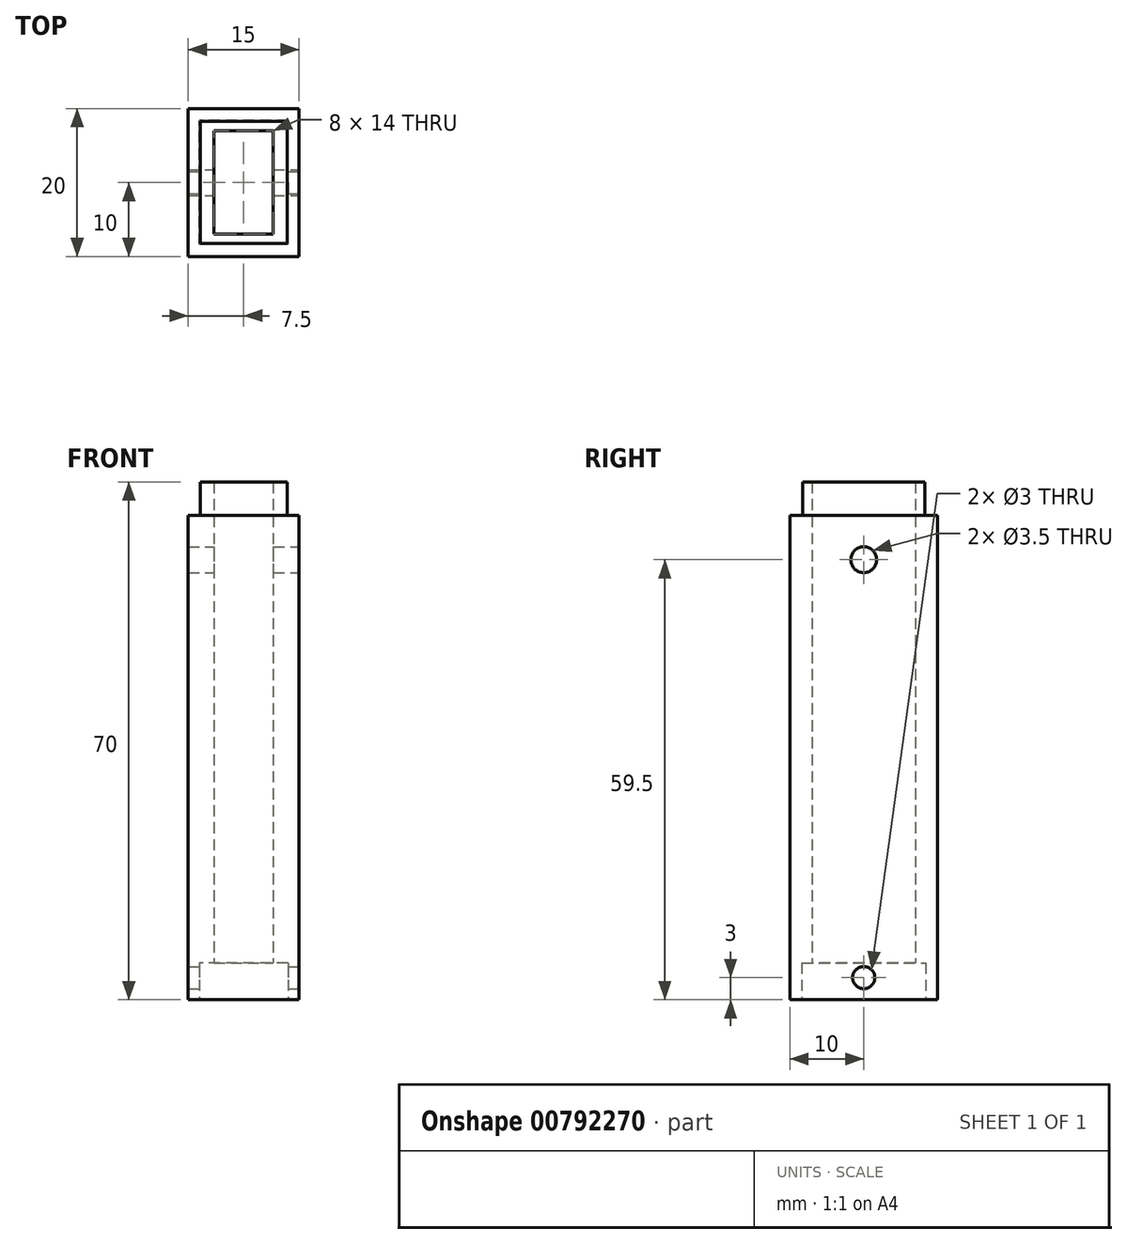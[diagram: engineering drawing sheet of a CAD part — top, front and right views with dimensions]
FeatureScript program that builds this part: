
annotation { "Feature Type Name" : "Feature", "Feature Type Description" : "" }
export const myFeature = defineFeature(function(context is Context, id is Id, definition is map)
    precondition{}
    {
        {
            var Q0;
            Q0=qCreatedBy(makeId("Top.planeOp"),FACE);
            var sketch = newSketch(context, id + "F0", { "sketchPlane" : qUnion([Q0])});
            skLineSegment(sketch, "E0.bottom", {"start": v(7.5, -10) * mm, "end": v(-7.5, -10) * mm});
            skLineSegment(sketch, "E0.top", {"start": v(7.5, 10) * mm, "end": v(-7.5, 10) * mm});
            skLineSegment(sketch, "E0.left", {"start": v(7.5, -10) * mm, "end": v(7.5, 10) * mm});
            skLineSegment(sketch, "E0.right", {"start": v(-7.5, -10) * mm, "end": v(-7.5, 10) * mm});
            skPoint(sketch, "E0.middle", {"position": v(0, 0) * mm});
            skLineSegment(sketch, "E1.bottom", {"start": v(4, -7) * mm, "end": v(-4, -7) * mm});
            skLineSegment(sketch, "E1.top", {"start": v(4, 7) * mm, "end": v(-4, 7) * mm});
            skLineSegment(sketch, "E1.left", {"start": v(4, -7) * mm, "end": v(4, 7) * mm});
            skLineSegment(sketch, "E1.right", {"start": v(-4, -7) * mm, "end": v(-4, 7) * mm});
            skSolve(sketch);
        }
        {
            var Q0;
            Q0 = qSketchRegion(id + "F0", true);
            extrude(context, id + "F1", {"entities" : qUnion([Q0]), "depth" : 70 * mm, "offsetDistance" : 25 * mm});
        }
        {
            var Q0;
            Q0=makeQuery(id+"F1.opExtrude","CAP_FACE",FACE,{"disambiguationData":[OSD([sQuery(id+"F0.wireOp",EDGE,"E0.bottom"),sQuery(id+"F0.wireOp",EDGE,"E0.top"),sQuery(id+"F0.wireOp",EDGE,"E0.left"),sQuery(id+"F0.wireOp",EDGE,"E0.right"),sQuery(id+"F0.wireOp",EDGE,"E1.bottom"),sQuery(id+"F0.wireOp",EDGE,"E1.top"),sQuery(id+"F0.wireOp",EDGE,"E1.left"),sQuery(id+"F0.wireOp",EDGE,"E1.right")])],"isStart":false});
            var sketch = newSketch(context, id + "F2", { "sketchPlane" : qUnion([Q0])});
            skLineSegment(sketch, "E2.bottom", {"start": v(5.88, 8.25) * mm, "end": v(-5.88, 8.25) * mm});
            skLineSegment(sketch, "E2.top", {"start": v(5.87, -8.25) * mm, "end": v(-5.88, -8.25) * mm});
            skLineSegment(sketch, "E2.left", {"start": v(5.88, 8.25) * mm, "end": v(5.87, -8.25) * mm});
            skLineSegment(sketch, "E2.right", {"start": v(-5.87, 8.25) * mm, "end": v(-5.88, -8.25) * mm});
            skPoint(sketch, "E2.middle", {"position": v(0, 0) * mm});
            skLineSegment(sketch, "E3.bottom", {"start": v(9.2, 12.25) * mm, "end": v(-9.2, 12.25) * mm});
            skLineSegment(sketch, "E3.top", {"start": v(9.2, -12.25) * mm, "end": v(-9.2, -12.25) * mm});
            skLineSegment(sketch, "E3.left", {"start": v(9.2, 12.25) * mm, "end": v(9.2, -12.25) * mm});
            skLineSegment(sketch, "E3.right", {"start": v(-9.2, 12.25) * mm, "end": v(-9.2, -12.25) * mm});
            skSolve(sketch);
        }
        {
            var Q0;
            Q0 = qSketchRegion(id + "F2", true);
            extrude(context, id + "F3", {"entities" : qUnion([Q0]), "operationType" : NewBodyOperationType.REMOVE, "oppositeDirection" : true, "depth" : 4.5 * mm, "offsetDistance" : 25 * mm});
        }
        {
            var Q0;
            Q0=makeQuery(id+"F1.opExtrude","SWEPT_FACE",FACE,{"disambiguationData":[OSD([sQuery(id+"F0.wireOp",EDGE,"E0.left")])]});
            var sketch = newSketch(context, id + "F4", { "sketchPlane" : qUnion([Q0])});
            skCircle(sketch, "E4", {"center": v(0, 59.5) * mm, "radius": 1.75 * mm});
            skCircle(sketch, "E5", {"center": v(0, 3) * mm, "radius": 1.5 * mm});
            skSolve(sketch);
        }
        {
            var Q0;
            Q0 = qSketchRegion(id + "F4", true);
            extrude(context, id + "F5", {"entities" : qUnion([Q0]), "operationType" : NewBodyOperationType.REMOVE, "oppositeDirection" : true, "depth" : 25 * mm, "offsetDistance" : 25 * mm});
        }
        {
            var Q0;
            Q0=makeQuery(id+"F1.opExtrude","CAP_FACE",FACE,{"disambiguationData":[OSD([sQuery(id+"F0.wireOp",EDGE,"E0.bottom"),sQuery(id+"F0.wireOp",EDGE,"E0.top"),sQuery(id+"F0.wireOp",EDGE,"E0.left"),sQuery(id+"F0.wireOp",EDGE,"E0.right"),sQuery(id+"F0.wireOp",EDGE,"E1.bottom"),sQuery(id+"F0.wireOp",EDGE,"E1.top"),sQuery(id+"F0.wireOp",EDGE,"E1.left"),sQuery(id+"F0.wireOp",EDGE,"E1.right")])],"isStart":true});
            var sketch = newSketch(context, id + "F6", { "sketchPlane" : qUnion([Q0])});
            skLineSegment(sketch, "E6.bottom", {"start": v(6, 8.38) * mm, "end": v(-6, 8.38) * mm});
            skLineSegment(sketch, "E6.top", {"start": v(6, -8.38) * mm, "end": v(-6, -8.38) * mm});
            skLineSegment(sketch, "E6.left", {"start": v(6, 8.38) * mm, "end": v(6, -8.38) * mm});
            skLineSegment(sketch, "E6.right", {"start": v(-6, 8.38) * mm, "end": v(-6, -8.38) * mm});
            skPoint(sketch, "E6.middle", {"position": v(0, 0) * mm});
            skSolve(sketch);
        }
        {
            var Q0;
            Q0 = qSketchRegion(id + "F6", true);
            extrude(context, id + "F7", {"entities" : qUnion([Q0]), "operationType" : NewBodyOperationType.REMOVE, "oppositeDirection" : true, "depth" : 5 * mm, "offsetDistance" : 25 * mm});
        }
    });
